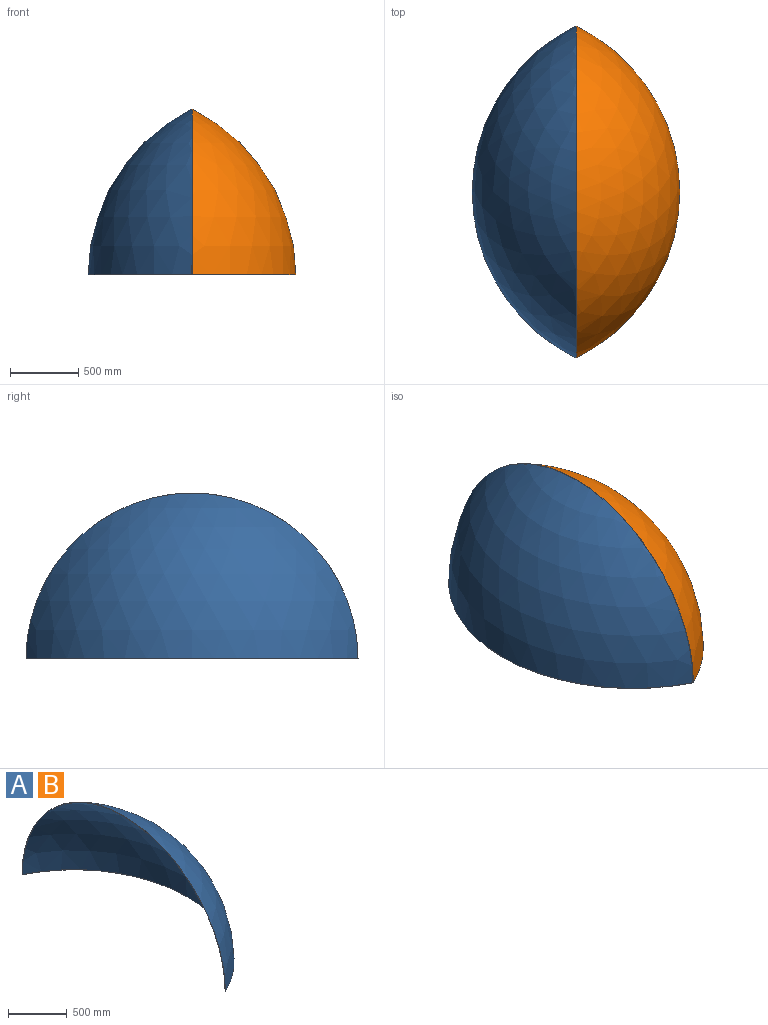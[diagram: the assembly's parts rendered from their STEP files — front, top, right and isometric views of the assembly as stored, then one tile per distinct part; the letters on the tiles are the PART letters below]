
ASSEMBLY  parts=2 mates=1
PART A: 4 faces, bbox 1099.7x2438.4x1223.4 mm
  f0: plane 2438.4x1219.2mm, normal (-1,0,0), area 13513.3mm2, adj f1,f2,f3
  f1: plane 2438.4x762mm, normal (0,0,-1), area 9606.1mm2, adj f0,f2,f3
  f2: sphere r=1356.36mm, area 3246982.7mm2, adj f0,f1
  f3: sphere r=1353.19mm, area 3225884.6mm2, adj f0,f1
PART B: same geometry as A
PLACE A rot(axis=(0,0,1),180deg) t=(0,0,0)mm
PLACE B at identity fixed
MATE fastened B.f1 <-> A.f1  axis (0,0,1) through (0,0,0)mm
